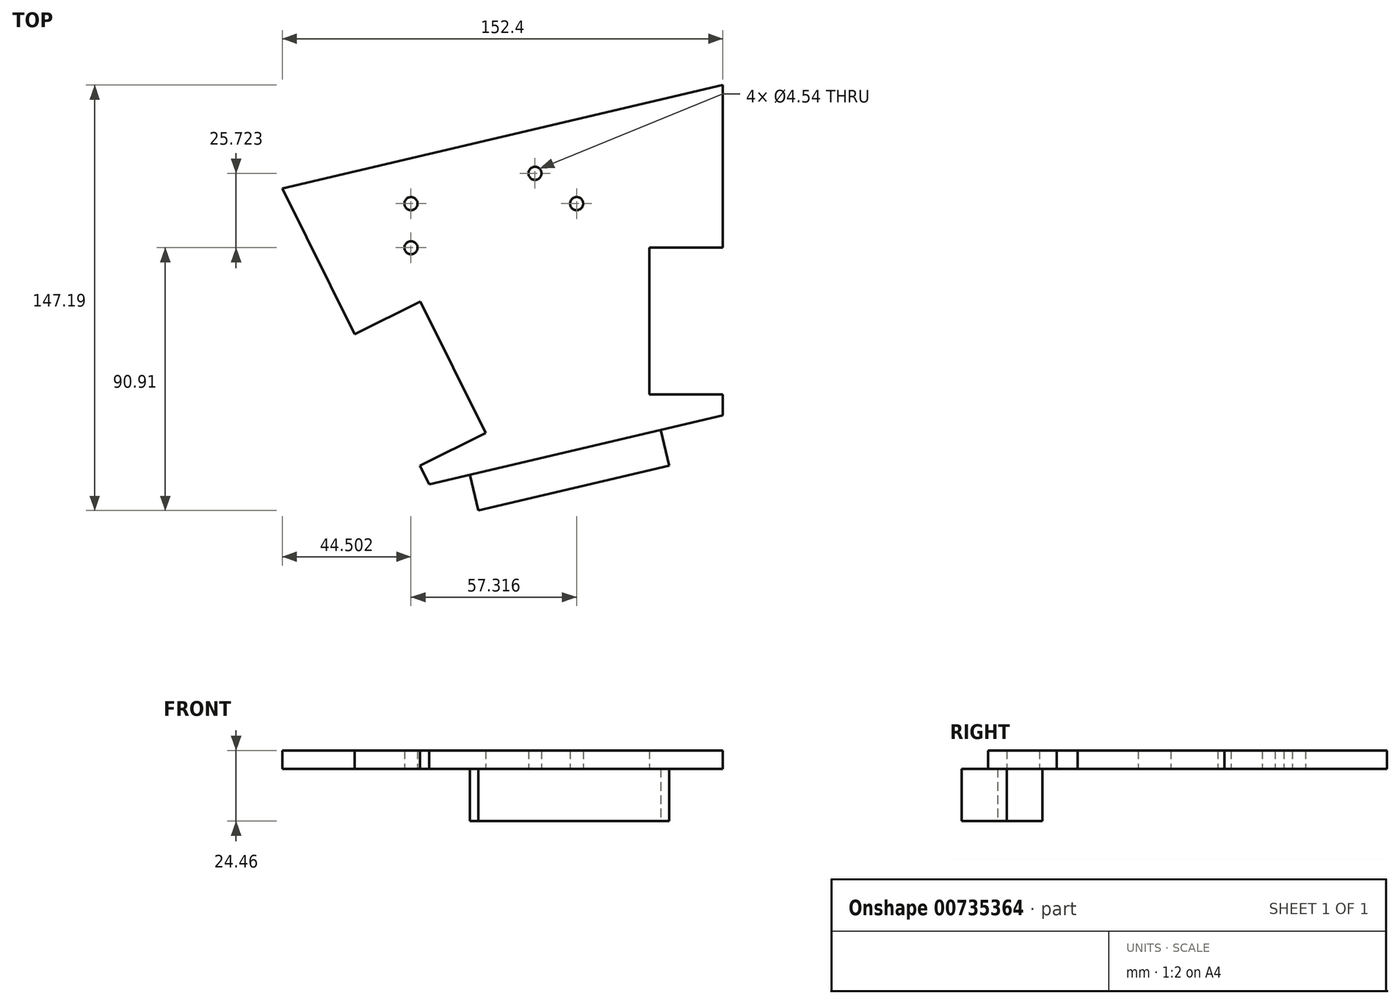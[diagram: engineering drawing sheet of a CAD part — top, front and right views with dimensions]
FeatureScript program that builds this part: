
annotation { "Feature Type Name" : "Feature", "Feature Type Description" : "" }
export const myFeature = defineFeature(function(context is Context, id is Id, definition is map)
    precondition{}
    {
        {
            var Q0;
            Q0=qCreatedBy(makeId("Top.planeOp"),FACE);
            var sketch = newSketch(context, id + "F0", { "sketchPlane" : qUnion([Q0])});
            skLineSegment(sketch, "E0", {"start": v(-74.2, 20.55) * mm, "end": v(78.2, 56.28) * mm});
            skLineSegment(sketch, "E1", {"start": v(-23.4, -81.84) * mm, "end": v(78.2, -58.02) * mm});
            skLineSegment(sketch, "E2", {"start": v(78.2, -58.02) * mm, "end": v(78.2, -50.8) * mm});
            skLineSegment(sketch, "E3", {"start": v(78.2, 0) * mm, "end": v(52.8, 0) * mm});
            skLineSegment(sketch, "E4", {"start": v(52.8, 0) * mm, "end": v(52.8, -50.8) * mm});
            skLineSegment(sketch, "E5", {"start": v(52.8, -50.8) * mm, "end": v(78.2, -50.8) * mm});
            skLineSegment(sketch, "E6.trimOffspring", {"start": v(78.2, 0) * mm, "end": v(78.2, 56.28) * mm});
            skLineSegment(sketch, "E7.trimOffspring", {"start": v(-49.19, -29.86) * mm, "end": v(-74.2, 20.55) * mm});
            skLineSegment(sketch, "E8", {"start": v(-26.6, -75.37) * mm, "end": v(-23.4, -81.84) * mm});
            skLineSegment(sketch, "E9", {"start": v(-49.19, -29.86) * mm, "end": v(-26.43, -18.57) * mm});
            skLineSegment(sketch, "E10", {"start": v(-26.43, -18.57) * mm, "end": v(-3.86, -64.08) * mm});
            skLineSegment(sketch, "E11", {"start": v(-26.6, -75.37) * mm, "end": v(-3.86, -64.08) * mm});
            skCircle(sketch, "E12", {"center": v(-29.7, 15.27) * mm, "radius": 2.27 * mm});
            skCircle(sketch, "E13", {"center": v(-29.7, 0) * mm, "radius": 2.27 * mm});
            skCircle(sketch, "E14", {"center": v(13.22, 25.72) * mm, "radius": 2.27 * mm});
            skCircle(sketch, "E15", {"center": v(27.62, 15.27) * mm, "radius": 2.27 * mm});
            skLineSegment(sketch, "E16", {"start": v(2, 38.42) * mm, "end": v(27.4, -69.93) * mm});
            skSolve(sketch);
        }
        {
            var Q0;
            Q0=makeQuery(id+"F0.imprint","IMPRINT",FACE,{"disambiguationData":[TD([[makeQuery(id+"F0.imprint","IMPRINT",EDGE,{"derivedFrom":sQuery(id+"F0.wireOp",EDGE,"E0")}),-1.0]])]});
            extrude(context, id + "F1", {"entities" : qUnion([Q0]), "depth" : 6.35 * mm, "offsetDistance" : 25.4 * mm});
        }
        {
            var Q0;
            Q0=makeQuery(id+"F1.opExtrude","SWEPT_FACE",FACE,{"disambiguationData":[OSD([sQuery(id+"F0.wireOp",EDGE,"E1")])]});
            var sketch = newSketch(context, id + "F2", { "sketchPlane" : qUnion([Q0])});
            skLineSegment(sketch, "E17.bottom", {"start": v(-27.02, 6.35) * mm, "end": v(40.89, 6.35) * mm});
            skLineSegment(sketch, "E17.top", {"start": v(-27.02, -18.11) * mm, "end": v(40.89, -18.11) * mm});
            skLineSegment(sketch, "E17.left", {"start": v(-27.02, 6.35) * mm, "end": v(-27.02, -18.11) * mm});
            skLineSegment(sketch, "E17.right", {"start": v(40.89, 6.35) * mm, "end": v(40.89, -18.11) * mm});
            skSolve(sketch);
        }
        {
            var Q0;
            {var subQ0=sQuery(id+"F2.wireOp",EDGE,"E17.top");Q0=makeQuery(id+"F2.imprint","IMPRINT",FACE,{"disambiguationData":[TD([[makeQuery(id+"F2.imprint","IMPRINT",EDGE,{"derivedFrom":subQ0}),1.0]])]});}
            extrude(context, id + "F3", {"entities" : qUnion([Q0]), "depth" : 12.7 * mm, "offsetDistance" : 25.4 * mm});
        }
    });
